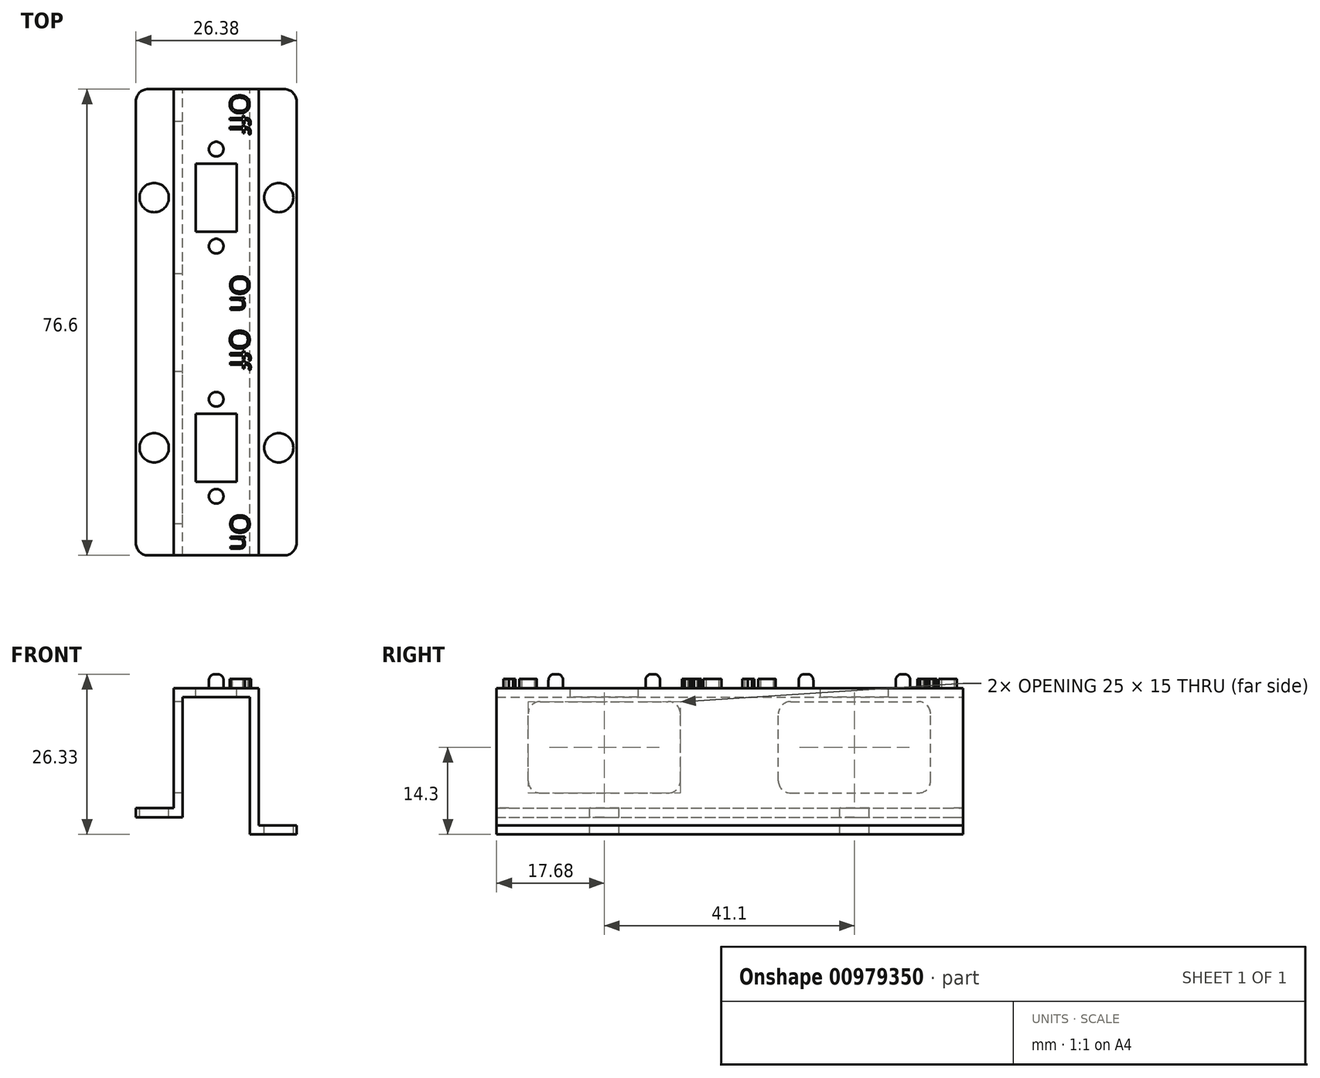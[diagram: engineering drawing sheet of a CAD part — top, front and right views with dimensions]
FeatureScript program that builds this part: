
annotation { "Feature Type Name" : "Feature", "Feature Type Description" : "" }
export const myFeature = defineFeature(function(context is Context, id is Id, definition is map)
    precondition{}
    {
        {
            var Q0;
            Q0=qCreatedBy(makeId("Front.planeOp"),FACE);
            var sketch = newSketch(context, id + "F0", { "sketchPlane" : qUnion([Q0])});
            skLineSegment(sketch, "E0", {"start": v(0, 0) * mm, "end": v(0, 1.5) * mm});
            skLineSegment(sketch, "E1", {"start": v(0, 1.5) * mm, "end": v(6.19, 1.5) * mm});
            skLineSegment(sketch, "E2", {"start": v(6.19, 1.5) * mm, "end": v(6.19, 21.23) * mm});
            skLineSegment(sketch, "E3", {"start": v(6.19, 21.23) * mm, "end": v(20.2, 21.23) * mm});
            skLineSegment(sketch, "E4", {"start": v(20.2, 21.23) * mm, "end": v(20.2, -1.3) * mm});
            skLineSegment(sketch, "E5", {"start": v(20.2, -1.3) * mm, "end": v(26.38, -1.3) * mm});
            skLineSegment(sketch, "E6", {"start": v(26.38, -1.3) * mm, "end": v(26.38, -2.8) * mm});
            skLineSegment(sketch, "E7", {"start": v(26.38, -2.8) * mm, "end": v(18.7, -2.8) * mm});
            skLineSegment(sketch, "E8", {"start": v(18.7, -2.8) * mm, "end": v(18.7, 19.73) * mm});
            skLineSegment(sketch, "E9", {"start": v(18.7, 19.73) * mm, "end": v(7.69, 19.73) * mm});
            skLineSegment(sketch, "E10", {"start": v(7.69, 19.73) * mm, "end": v(7.69, 0) * mm});
            skLineSegment(sketch, "E11", {"start": v(7.7, 0) * mm, "end": v(0, 0) * mm});
            skSolve(sketch);
        }
        {
            var Q0;
            Q0=makeQuery(id+"F0.imprint","IMPRINT",FACE,{"disambiguationData":[TD([[makeQuery(id+"F0.imprint","IMPRINT",EDGE,{"derivedFrom":sQuery(id+"F0.wireOp",EDGE,"E0")}),-1.0]])]});
            extrude(context, id + "F1", {"entities" : qUnion([Q0]), "depth" : 76.6 * mm, "offsetDistance" : 25 * mm});
        }
        {
            var Q0;
            Q0=makeQuery(id+"F1.opExtrude","SWEPT_FACE",FACE,{"disambiguationData":[OSD([sQuery(id+"F0.wireOp",EDGE,"E1")])]});
            var sketch = newSketch(context, id + "F2", { "sketchPlane" : qUnion([Q0])});
            skCircle(sketch, "E12", {"center": v(3, -17.82) * mm, "radius": 2.4 * mm});
            skCircle(sketch, "E13", {"center": v(3, -58.92) * mm, "radius": 2.4 * mm});
            skCircle(sketch, "E14", {"center": v(23.47, -17.82) * mm, "radius": 2.4 * mm});
            skCircle(sketch, "E15", {"center": v(23.47, -58.92) * mm, "radius": 2.4 * mm});
            skSolve(sketch);
        }
        {
            var Q0;
            Q0=makeQuery(id+"F2.imprint","IMPRINT",FACE,{"disambiguationData":[TD([[makeQuery(id+"F2.imprint","IMPRINT",EDGE,{"derivedFrom":sQuery(id+"F2.wireOp",EDGE,"E12")}),1.0]])]});
            var Q1;
            Q1=makeQuery(id+"F2.imprint","IMPRINT",FACE,{"disambiguationData":[TD([[makeQuery(id+"F2.imprint","IMPRINT",EDGE,{"derivedFrom":sQuery(id+"F2.wireOp",EDGE,"E13")}),1.0]])]});
            var Q2;
            Q2=makeQuery(id+"F2.imprint","IMPRINT",FACE,{"disambiguationData":[TD([[makeQuery(id+"F2.imprint","IMPRINT",EDGE,{"derivedFrom":sQuery(id+"F2.wireOp",EDGE,"E15")}),1.0]])]});
            var Q3;
            Q3=makeQuery(id+"F2.imprint","IMPRINT",FACE,{"disambiguationData":[TD([[makeQuery(id+"F2.imprint","IMPRINT",EDGE,{"derivedFrom":sQuery(id+"F2.wireOp",EDGE,"E14")}),1.0]])]});
            extrude(context, id + "F3", {"entities" : qUnion([Q0, Q1, Q2, Q3]), "operationType" : NewBodyOperationType.REMOVE, "oppositeDirection" : true, "depth" : 10 * mm, "offsetDistance" : 25 * mm});
        }
        {
            var Q0;
            Q0=makeQuery(id+"F1.opExtrude","SWEPT_FACE",FACE,{"disambiguationData":[OSD([sQuery(id+"F0.wireOp",EDGE,"E2")])]});
            var sketch = newSketch(context, id + "F4", { "sketchPlane" : qUnion([Q0])});
            skLineSegment(sketch, "E16.bottom", {"start": v(30.32, 4) * mm, "end": v(5.32, 4) * mm});
            skLineSegment(sketch, "E16.top", {"start": v(30.32, 19) * mm, "end": v(5.32, 19) * mm});
            skLineSegment(sketch, "E16.left", {"start": v(30.32, 4) * mm, "end": v(30.32, 19) * mm});
            skLineSegment(sketch, "E16.right", {"start": v(5.32, 4) * mm, "end": v(5.32, 19) * mm});
            skPoint(sketch, "E16.middle", {"position": v(17.82, 11.5) * mm});
            skLineSegment(sketch, "E17.bottom", {"start": v(71.42, 4) * mm, "end": v(46.42, 4) * mm});
            skLineSegment(sketch, "E17.top", {"start": v(71.42, 19) * mm, "end": v(46.42, 19) * mm});
            skLineSegment(sketch, "E17.left", {"start": v(71.42, 4) * mm, "end": v(71.42, 19) * mm});
            skLineSegment(sketch, "E17.right", {"start": v(46.42, 4) * mm, "end": v(46.42, 19) * mm});
            skPoint(sketch, "E17.middle", {"position": v(58.92, 11.5) * mm});
            skSolve(sketch);
        }
        {
            var Q0;
            Q0=makeQuery(id+"F4.imprint","IMPRINT",FACE,{"disambiguationData":[TD([[makeQuery(id+"F4.imprint","IMPRINT",EDGE,{"derivedFrom":sQuery(id+"F4.wireOp",EDGE,"E16.bottom")}),-1.0]])]});
            var Q1;
            Q1=makeQuery(id+"F4.imprint","IMPRINT",FACE,{"disambiguationData":[TD([[makeQuery(id+"F4.imprint","IMPRINT",EDGE,{"derivedFrom":sQuery(id+"F4.wireOp",EDGE,"E17.bottom")}),-1.0]])]});
            extrude(context, id + "F5", {"entities" : qUnion([Q0, Q1]), "operationType" : NewBodyOperationType.REMOVE, "endBound" : BoundingType.UP_TO_NEXT, "oppositeDirection" : true, "depth" : 25 * mm, "offsetDistance" : 25 * mm});
        }
        {
            var Q0;
            Q0=makeQuery(id+"F1.opExtrude","SWEPT_FACE",FACE,{"disambiguationData":[OSD([sQuery(id+"F0.wireOp",EDGE,"E3")])]});
            var sketch = newSketch(context, id + "F6", { "sketchPlane" : qUnion([Q0])});
            skLineSegment(sketch, "E18", {"start": v(13.2, 0) * mm, "end": v(13.2, -86.72) * mm, "construction": true});
            skLineSegment(sketch, "E19.bottom", {"start": v(16.54, -12.22) * mm, "end": v(9.84, -12.22) * mm});
            skLineSegment(sketch, "E19.top", {"start": v(16.54, -23.42) * mm, "end": v(9.84, -23.42) * mm});
            skLineSegment(sketch, "E19.left", {"start": v(16.54, -12.22) * mm, "end": v(16.54, -23.42) * mm});
            skLineSegment(sketch, "E19.right", {"start": v(9.84, -12.22) * mm, "end": v(9.84, -23.42) * mm});
            skPoint(sketch, "E19.middle", {"position": v(13.2, -17.82) * mm});
            skLineSegment(sketch, "E20.bottom", {"start": v(16.54, -53.32) * mm, "end": v(9.84, -53.32) * mm});
            skLineSegment(sketch, "E20.top", {"start": v(16.54, -64.52) * mm, "end": v(9.84, -64.52) * mm});
            skLineSegment(sketch, "E20.left", {"start": v(16.54, -53.32) * mm, "end": v(16.54, -64.52) * mm});
            skLineSegment(sketch, "E20.right", {"start": v(9.84, -53.32) * mm, "end": v(9.84, -64.52) * mm});
            skPoint(sketch, "E20.middle", {"position": v(13.2, -58.92) * mm});
            skSolve(sketch);
        }
        {
            var Q0;
            Q0=makeQuery(id+"F6.imprint","IMPRINT",FACE,{"disambiguationData":[TD([[makeQuery(id+"F6.imprint","IMPRINT",EDGE,{"derivedFrom":sQuery(id+"F6.wireOp",EDGE,"E19.bottom")}),1.0]])]});
            var Q1;
            Q1=makeQuery(id+"F6.imprint","IMPRINT",FACE,{"disambiguationData":[TD([[makeQuery(id+"F6.imprint","IMPRINT",EDGE,{"derivedFrom":sQuery(id+"F6.wireOp",EDGE,"E20.bottom")}),1.0]])]});
            extrude(context, id + "F7", {"entities" : qUnion([Q0, Q1]), "operationType" : NewBodyOperationType.REMOVE, "endBound" : BoundingType.UP_TO_NEXT, "oppositeDirection" : true, "depth" : 25 * mm, "offsetDistance" : 25 * mm});
        }
        {
            var Q0;
            Q0=makeQuery(id+"F1.opExtrude","SWEPT_FACE",FACE,{"disambiguationData":[OSD([sQuery(id+"F0.wireOp",EDGE,"E3")])]});
            var sketch = newSketch(context, id + "F8", { "sketchPlane" : qUnion([Q0])});
            skCircle(sketch, "E21", {"center": v(13.19, -66.89) * mm, "radius": 1.2 * mm});
            skPoint(sketch, "E21.centerSnap0", {"position": v(13.19, -64.52) * mm});
            skCircle(sketch, "E22", {"center": v(13.19, -50.95) * mm, "radius": 1.2 * mm});
            skPoint(sketch, "E22.centerSnap0", {"position": v(13.19, -53.32) * mm});
            skCircle(sketch, "E23", {"center": v(13.19, -25.8) * mm, "radius": 1.2 * mm});
            skPoint(sketch, "E23.centerSnap0", {"position": v(13.19, -23.42) * mm});
            skCircle(sketch, "E24", {"center": v(13.19, -9.85) * mm, "radius": 1.2 * mm});
            skPoint(sketch, "E24.centerSnap0", {"position": v(13.19, -12.22) * mm});
            skSolve(sketch);
        }
        {
            var Q0;
            Q0=makeQuery(id+"F8.imprint","IMPRINT",FACE,{"disambiguationData":[TD([[makeQuery(id+"F8.imprint","IMPRINT",EDGE,{"derivedFrom":sQuery(id+"F8.wireOp",EDGE,"E24")}),1.0]])]});
            var Q1;
            Q1=makeQuery(id+"F8.imprint","IMPRINT",FACE,{"disambiguationData":[TD([[makeQuery(id+"F8.imprint","IMPRINT",EDGE,{"derivedFrom":sQuery(id+"F8.wireOp",EDGE,"E23")}),1.0]])]});
            var Q2;
            Q2=makeQuery(id+"F8.imprint","IMPRINT",FACE,{"disambiguationData":[TD([[makeQuery(id+"F8.imprint","IMPRINT",EDGE,{"derivedFrom":sQuery(id+"F8.wireOp",EDGE,"E22")}),1.0]])]});
            var Q3;
            Q3=makeQuery(id+"F8.imprint","IMPRINT",FACE,{"disambiguationData":[TD([[makeQuery(id+"F8.imprint","IMPRINT",EDGE,{"derivedFrom":sQuery(id+"F8.wireOp",EDGE,"E21")}),1.0]])]});
            extrude(context, id + "F9", {"entities" : qUnion([Q0, Q1, Q2, Q3]), "operationType" : NewBodyOperationType.ADD, "depth" : 2.3 * mm, "offsetDistance" : 25 * mm});
        }
        {
            var Q0;
            Q0=makeQuery(id+"F9.opExtrude","CAP_EDGE",EDGE,{"disambiguationData":[OSD([sQuery(id+"F8.wireOp",EDGE,"E24")])],"isStart":false});
            var Q1;
            Q1=makeQuery(id+"F9.opExtrude","CAP_EDGE",EDGE,{"disambiguationData":[OSD([sQuery(id+"F8.wireOp",EDGE,"E23")])],"isStart":false});
            var Q2;
            Q2=makeQuery(id+"F9.opExtrude","CAP_EDGE",EDGE,{"disambiguationData":[OSD([sQuery(id+"F8.wireOp",EDGE,"E22")])],"isStart":false});
            var Q3;
            Q3=makeQuery(id+"F9.opExtrude","CAP_EDGE",EDGE,{"disambiguationData":[OSD([sQuery(id+"F8.wireOp",EDGE,"E21")])],"isStart":false});
            fillet(context, id + "F10", {"entities" : qUnion([Q0, Q1, Q2, Q3]), "radius" : 1 * mm, "tangentPropagation" : true, "allowEdgeOverflow" : false});
        }
        {
            var Q0;
            Q0=makeQuery(id+"F5.boolean.opBoolean","COPY",EDGE,{"derivedFrom":makeQuery(id+"F5.opExtrude","SWEPT_EDGE",EDGE,{"disambiguationData":[OSD([sQuery(id+"F4.wireOp",EDGE,"E16.bottom"),sQuery(id+"F4.wireOp",EDGE,"E16.right")])]})});
            var Q1;
            Q1=makeQuery(id+"F5.boolean.opBoolean","COPY",EDGE,{"derivedFrom":makeQuery(id+"F5.opExtrude","SWEPT_EDGE",EDGE,{"disambiguationData":[OSD([sQuery(id+"F4.wireOp",EDGE,"E16.top"),sQuery(id+"F4.wireOp",EDGE,"E16.right")])]})});
            var Q2;
            Q2=makeQuery(id+"F5.boolean.opBoolean","COPY",EDGE,{"derivedFrom":makeQuery(id+"F5.opExtrude","SWEPT_EDGE",EDGE,{"disambiguationData":[OSD([sQuery(id+"F4.wireOp",EDGE,"E16.top"),sQuery(id+"F4.wireOp",EDGE,"E16.left")])]})});
            var Q3;
            Q3=makeQuery(id+"F5.boolean.opBoolean","COPY",EDGE,{"derivedFrom":makeQuery(id+"F5.opExtrude","SWEPT_EDGE",EDGE,{"disambiguationData":[OSD([sQuery(id+"F4.wireOp",EDGE,"E16.bottom"),sQuery(id+"F4.wireOp",EDGE,"E16.left")])]})});
            var Q4;
            Q4=makeQuery(id+"F5.boolean.opBoolean","COPY",EDGE,{"derivedFrom":makeQuery(id+"F5.opExtrude","SWEPT_EDGE",EDGE,{"disambiguationData":[OSD([sQuery(id+"F4.wireOp",EDGE,"E17.top"),sQuery(id+"F4.wireOp",EDGE,"E17.right")])]})});
            var Q5;
            Q5=makeQuery(id+"F5.boolean.opBoolean","COPY",EDGE,{"derivedFrom":makeQuery(id+"F5.opExtrude","SWEPT_EDGE",EDGE,{"disambiguationData":[OSD([sQuery(id+"F4.wireOp",EDGE,"E17.bottom"),sQuery(id+"F4.wireOp",EDGE,"E17.right")])]})});
            var Q6;
            Q6=makeQuery(id+"F5.boolean.opBoolean","COPY",EDGE,{"derivedFrom":makeQuery(id+"F5.opExtrude","SWEPT_EDGE",EDGE,{"disambiguationData":[OSD([sQuery(id+"F4.wireOp",EDGE,"E17.top"),sQuery(id+"F4.wireOp",EDGE,"E17.left")])]})});
            var Q7;
            Q7=makeQuery(id+"F5.boolean.opBoolean","COPY",EDGE,{"derivedFrom":makeQuery(id+"F5.opExtrude","SWEPT_EDGE",EDGE,{"disambiguationData":[OSD([sQuery(id+"F4.wireOp",EDGE,"E17.bottom"),sQuery(id+"F4.wireOp",EDGE,"E17.left")])]})});
            fillet(context, id + "F11", {"entities" : qUnion([Q0, Q1, Q2, Q3, Q4, Q5, Q6, Q7]), "radius" : 2 * mm, "tangentPropagation" : true, "allowEdgeOverflow" : false});
        }
        {
            var Q0;
            Q0=makeQuery(id+"F1.opExtrude","CAP_EDGE",EDGE,{"disambiguationData":[OSD([sQuery(id+"F0.wireOp",EDGE,"E6")])],"isStart":true});
            var Q1;
            Q1=makeQuery(id+"F1.opExtrude","CAP_EDGE",EDGE,{"disambiguationData":[OSD([sQuery(id+"F0.wireOp",EDGE,"E0")])],"isStart":true});
            var Q2;
            Q2=makeQuery(id+"F1.opExtrude","CAP_EDGE",EDGE,{"disambiguationData":[OSD([sQuery(id+"F0.wireOp",EDGE,"E6")])],"isStart":false});
            var Q3;
            Q3=makeQuery(id+"F1.opExtrude","CAP_EDGE",EDGE,{"disambiguationData":[OSD([sQuery(id+"F0.wireOp",EDGE,"E0")])],"isStart":false});
            fillet(context, id + "F12", {"entities" : qUnion([Q0, Q1, Q2, Q3]), "radius" : 2 * mm, "tangentPropagation" : true, "allowEdgeOverflow" : false});
        }
        {
            var Q0;
            Q0=makeQuery(id+"F1.opExtrude","SWEPT_FACE",FACE,{"disambiguationData":[OSD([sQuery(id+"F0.wireOp",EDGE,"E3")])]});
            var sketch = newSketch(context, id + "F13", { "sketchPlane" : qUnion([Q0])});
            skText(sketch, "E25", { "text": "Off", "fontName": "OpenSans-Regular.ttf"});
            skText(sketch, "E26", { "text": "On", "fontName": "OpenSans-Regular.ttf"});
            skText(sketch, "E27", { "text": "Off", "fontName": "OpenSans-Regular.ttf"});
            skText(sketch, "E28", { "text": "On", "fontName": "OpenSans-Regular.ttf"});
            const initialGuessF13  = {"E25": [0.01546, -0.03942, 0, -1, 0.00322], "E26": [0.01554, -0.06975, 0, -1, 0.00314], "E27": [0.01544, -0.00075, 0, -1, 0.00322], "E28": [0.01552, -0.0305, 0, -1, 0.00314]};
            skSetInitialGuess(sketch, initialGuessF13);
            skSolve(sketch);
        }
        {
            var Q0;
            Q0 = qSketchRegion(id + "F13", true);
            extrude(context, id + "F14", {"entities" : qUnion([Q0]), "operationType" : NewBodyOperationType.ADD, "depth" : 1.5 * mm, "offsetDistance" : 25 * mm});
        }
    });
